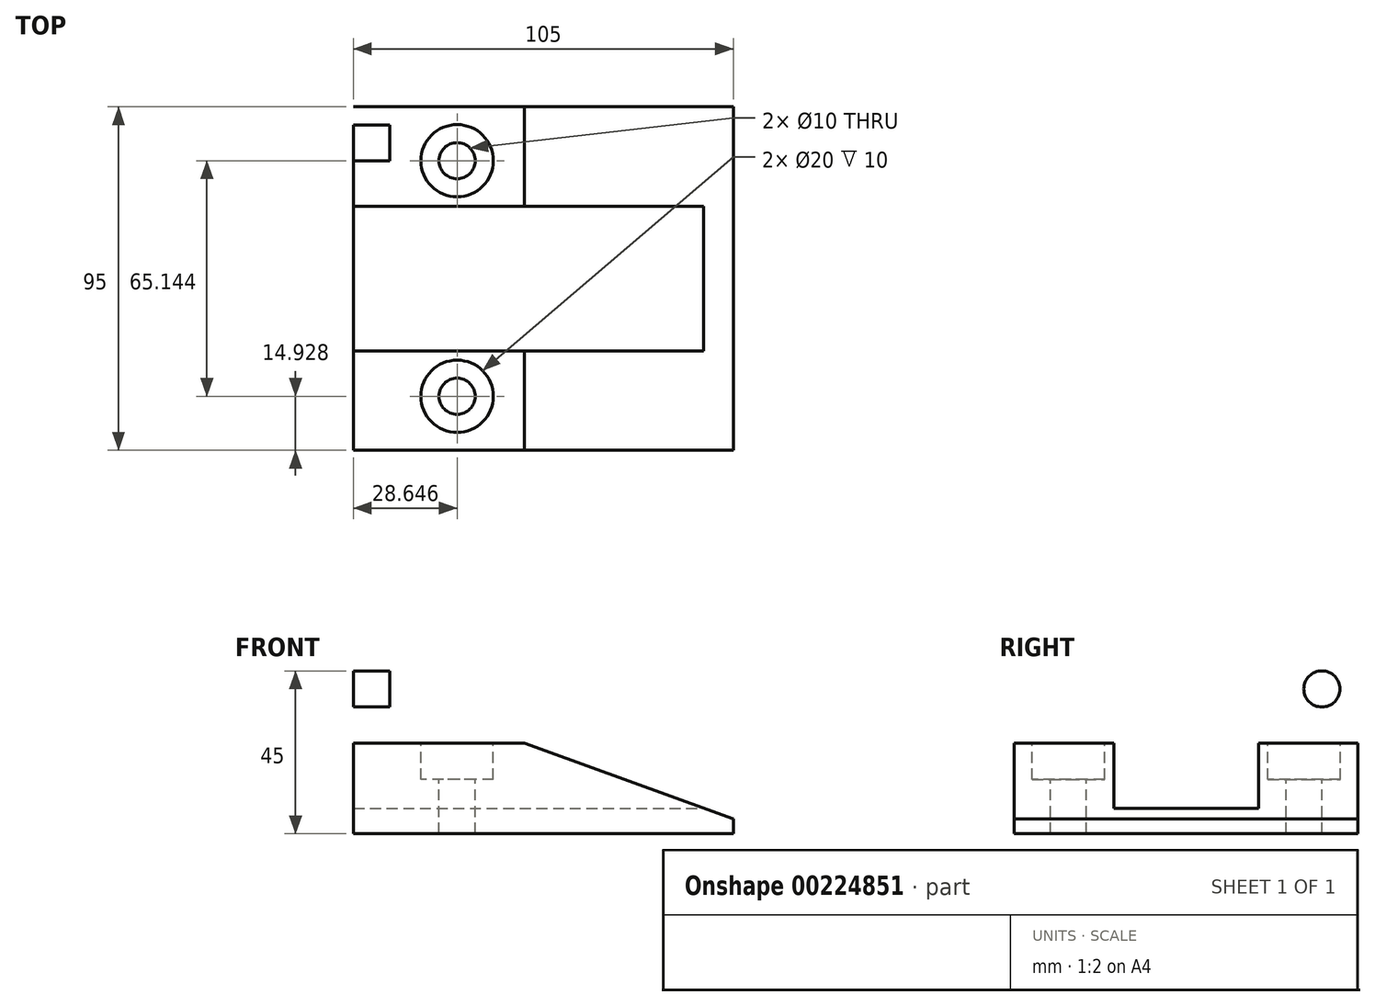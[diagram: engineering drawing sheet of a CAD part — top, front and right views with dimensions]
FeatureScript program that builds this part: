
annotation { "Feature Type Name" : "Feature", "Feature Type Description" : "" }
export const myFeature = defineFeature(function(context is Context, id is Id, definition is map)
    precondition{}
    {
        {
            var Q0;
            Q0=qCreatedBy(makeId("Top.planeOp"),FACE);
            var sketch = newSketch(context, id + "F0", { "sketchPlane" : qUnion([Q0])});
            skLineSegment(sketch, "E0.bottom", {"start": v(-10.05, 47.5) * mm, "end": v(-0.05, 47.5) * mm});
            skLineSegment(sketch, "E0.top", {"start": v(-10.05, -47.5) * mm, "end": v(-0.05, -47.5) * mm});
            skLineSegment(sketch, "E0.left", {"start": v(-10.05, 47.5) * mm, "end": v(-10.05, -47.5) * mm});
            skLineSegment(sketch, "E0.right", {"start": v(-0.05, 47.5) * mm, "end": v(-0.05, -47.5) * mm});
            skPoint(sketch, "E0.middle", {"position": v(-5.05, 0) * mm});
            skPoint(sketch, "E1.0", {"position": v(0, 0) * mm});
            skLineSegment(sketch, "E2", {"start": v(-3.1, 0) * mm, "end": v(-3.1, -20) * mm, "construction": true});
            skLineSegment(sketch, "E3.bottom", {"start": v(-0.05, -20) * mm, "end": v(37.25, -20) * mm});
            skLineSegment(sketch, "E3.top", {"start": v(-0.05, -47.5) * mm, "end": v(37.25, -47.5) * mm});
            skLineSegment(sketch, "E3.left", {"start": v(-0.05, -20) * mm, "end": v(-0.05, -47.5) * mm});
            skLineSegment(sketch, "E3.right", {"start": v(37.25, -20) * mm, "end": v(37.25, -47.5) * mm});
            skLineSegment(sketch, "E4", {"start": v(-3.1, 0) * mm, "end": v(63.94, 0) * mm, "construction": true});
            skLineSegment(sketch, "E5.MirrorCS", {"start": v(-0.05, 20) * mm, "end": v(37.25, 20) * mm});
            skLineSegment(sketch, "E6.MirrorCS", {"start": v(-0.05, 47.5) * mm, "end": v(37.25, 47.5) * mm});
            skLineSegment(sketch, "E7.MirrorCS", {"start": v(37.25, 20) * mm, "end": v(37.25, 47.5) * mm});
            skLineSegment(sketch, "E8", {"start": v(37.25, -47.5) * mm, "end": v(94.95, -47.5) * mm});
            skLineSegment(sketch, "E9.MirrorCS", {"start": v(37.25, 47.5) * mm, "end": v(94.95, 47.5) * mm});
            skLineSegment(sketch, "E10", {"start": v(94.95, 47.5) * mm, "end": v(94.95, -47.5) * mm});
            skLineSegment(sketch, "E11", {"start": v(-0.05, 32.57) * mm, "end": v(18.6, 32.57) * mm, "construction": true});
            skPoint(sketch, "E12", {"position": v(18.6, 32.57) * mm});
            skPoint(sketch, "E13.MirrorP", {"position": v(18.6, -32.57) * mm});
            skSolve(sketch);
        }
        {
            var Q0;
            {var subQ4=sQuery(id+"F0.wireOp",EDGE,"E0.bottom");Q0=makeQuery(id+"F0.imprint","IMPRINT",FACE,{"disambiguationData":[TD([[makeQuery(id+"F0.imprint","IMPRINT",EDGE,{"derivedFrom":subQ4}),-1.0]])]});}
            extrude(context, id + "F1", {"entities" : qUnion([Q0]), "depth" : 50 * mm});
        }
        {
            var Q0;
            {var subQ2=sQuery(id+"F0.wireOp",EDGE,"E3.bottom");Q0=makeQuery(id+"F0.imprint","IMPRINT",FACE,{"disambiguationData":[TD([[makeQuery(id+"F0.imprint","IMPRINT",EDGE,{"derivedFrom":subQ2}),-1.0]])]});}
            var Q1;
            {var subQ2=sQuery(id+"F0.wireOp",EDGE,"E5.MirrorCS");Q1=makeQuery(id+"F0.imprint","IMPRINT",FACE,{"disambiguationData":[TD([[makeQuery(id+"F0.imprint","IMPRINT",EDGE,{"derivedFrom":subQ2}),1.0]])]});}
            extrude(context, id + "F2", {"entities" : qUnion([Q0, Q1]), "operationType" : NewBodyOperationType.ADD, "depth" : 25 * mm});
        }
        {
            var Q0;
            {var subQ1=sQuery(id+"F0.wireOp",EDGE,"E3.bottom");Q0=makeQuery(id+"F0.imprint","IMPRINT",FACE,{"disambiguationData":[TD([[makeQuery(id+"F0.imprint","IMPRINT",EDGE,{"derivedFrom":subQ1}),1.0]])]});}
            extrude(context, id + "F3", {"entities" : qUnion([Q0]), "operationType" : NewBodyOperationType.ADD, "depth" : 4 * mm});
        }
        {
            var Q0;
            Q0=makeQuery(id+"F3.boolean.opBoolean","MERGE",FACE,{"derivedFrom":[makeQuery(id+"F2.boolean.opBoolean","MERGE",FACE,{"derivedFrom":[makeQuery(id+"F1.opExtrude","SWEPT_FACE",FACE,{"disambiguationData":[OSD([sQuery(id+"F0.wireOp",EDGE,"E0.top")])]}),makeQuery(id+"F2.opExtrude","SWEPT_FACE",FACE,{"disambiguationData":[OSD([sQuery(id+"F0.wireOp",EDGE,"E3.top")])]})]}),makeQuery(id+"F3.opExtrude","SWEPT_FACE",FACE,{"disambiguationData":[OSD([sQuery(id+"F0.wireOp",EDGE,"E8")])]})]});
            var sketch = newSketch(context, id + "F4", { "sketchPlane" : qUnion([Q0])});
            skLineSegment(sketch, "E14.0", {"start": v(-0.05, 25) * mm, "end": v(37.25, 25) * mm});
            skLineSegment(sketch, "E15.0", {"start": v(37.25, 4) * mm, "end": v(94.95, 4) * mm});
            skLineSegment(sketch, "E16", {"start": v(37.25, 25) * mm, "end": v(94.95, 4) * mm});
            skLineSegment(sketch, "E17", {"start": v(37.25, 25) * mm, "end": v(37.25, 4) * mm});
            skSolve(sketch);
        }
        {
            var Q0;
            Q0=makeQuery(id+"F4.imprint","IMPRINT",FACE,{"disambiguationData":[TD([[makeQuery(id+"F4.imprint","IMPRINT",EDGE,{"derivedFrom":sQuery(id+"F4.wireOp",EDGE,"E15.0")}),1.0]])]});
            extrude(context, id + "F5", {"entities" : qUnion([Q0]), "oppositeDirection" : true, "depth" : 27.5 * mm});
        }
        {
            var Q0;
            Q0=makeQuery(id+"F5.opExtrude","SWEPT_BODY",BODY,{"disambiguationData":[OSD([sQuery(id+"F4.wireOp",EDGE,"E15.0"),sQuery(id+"F4.wireOp",EDGE,"E16"),sQuery(id+"F4.wireOp",EDGE,"E17")])]});
            var Q1;
            Q1=qCreatedBy(makeId("Front.planeOp"),FACE);
            mirror(context, id + "F6", {"operationType" : NewBodyOperationType.ADD, "entities" : qUnion([Q0]), "mirrorPlane" : qUnion([Q1])});
        }
        {
            var Q0;
            Q0=makeQuery(id+"F1.opExtrude","CAP_EDGE",EDGE,{"disambiguationData":[OSD([sQuery(id+"F0.wireOp",EDGE,"E0.top")])],"isStart":false});
            var Q1;
            Q1=makeQuery(id+"F1.opExtrude","CAP_EDGE",EDGE,{"disambiguationData":[OSD([sQuery(id+"F0.wireOp",EDGE,"E0.bottom")])],"isStart":false});
            fillet(context, id + "F7", {"entities" : qUnion([Q0, Q1]), "radius" : 10 * mm, "tangentPropagation" : true, "allowEdgeOverflow" : false});
        }
        {
            var Q0;
            Q0=makeQuery(id+"F1.opExtrude","SWEPT_FACE",FACE,{"disambiguationData":[OSD([sQuery(id+"F0.wireOp",EDGE,"E0.right")])]});
            var sketch = newSketch(context, id + "F8", { "sketchPlane" : qUnion([Q0])});
            skLineSegment(sketch, "E18", {"start": v(0, 0) * mm, "end": v(0, 50) * mm, "construction": true});
            skArc(sketch, "E19.0", {"start": v(-37.5, 50) * mm, "mid": v(-44.57, 47.07) * mm, "end": v(-47.5, 40) * mm});
            skCircle(sketch, "E20", {"center": v(-37.5, 40) * mm, "radius": 5 * mm});
            skCircle(sketch, "E21.MirrorC", {"center": v(37.5, 40) * mm, "radius": 5 * mm});
            skSolve(sketch);
        }
        {
            var Q0;
            Q0=makeQuery(id+"F8.imprint","IMPRINT",FACE,{"disambiguationData":[TD([[makeQuery(id+"F8.imprint","IMPRINT",EDGE,{"derivedFrom":sQuery(id+"F8.wireOp",EDGE,"E20")}),1.0]])]});
            var Q1;
            Q1=makeQuery(id+"F8.imprint","IMPRINT",FACE,{"disambiguationData":[TD([[makeQuery(id+"F8.imprint","IMPRINT",EDGE,{"derivedFrom":sQuery(id+"F8.wireOp",EDGE,"E21.MirrorC")}),-1.0]])]});
            extrude(context, id + "F9", {"entities" : qUnion([Q0, Q1]), "operationType" : NewBodyOperationType.REMOVE, "oppositeDirection" : true, "depth" : 25 * mm});
        }
        {
            var Q0;
            Q0=makeQuery(id+"F3.opExtrude","CAP_FACE",FACE,{"disambiguationData":[OSD([sQuery(id+"F0.wireOp",EDGE,"E0.right"),sQuery(id+"F0.wireOp",EDGE,"E3.bottom"),sQuery(id+"F0.wireOp",EDGE,"E3.right"),sQuery(id+"F0.wireOp",EDGE,"E5.MirrorCS"),sQuery(id+"F0.wireOp",EDGE,"E7.MirrorCS"),sQuery(id+"F0.wireOp",EDGE,"E8"),sQuery(id+"F0.wireOp",EDGE,"E9.MirrorCS"),sQuery(id+"F0.wireOp",EDGE,"E10")])],"isStart":false});
            var sketch = newSketch(context, id + "F10", { "sketchPlane" : qUnion([Q0])});
            skLineSegment(sketch, "E22.0", {"start": v(-0.05, 20) * mm, "end": v(94.95, 20) * mm});
            skLineSegment(sketch, "E22.1", {"start": v(-0.05, -20) * mm, "end": v(94.95, -20) * mm});
            skLineSegment(sketch, "E23", {"start": v(86.7, 20) * mm, "end": v(86.7, -20) * mm});
            skSolve(sketch);
        }
        {
            var Q0;
            Q0=makeQuery(id+"F6.boolean.opBoolean","MERGE",FACE,{"derivedFrom":[makeQuery(id+"F2.opExtrude","SWEPT_FACE",FACE,{"disambiguationData":[OSD([sQuery(id+"F0.wireOp",EDGE,"E3.bottom")])]}),makeQuery(id+"F5.opExtrude","CAP_FACE",FACE,{"disambiguationData":[OSD([sQuery(id+"F4.wireOp",EDGE,"E15.0"),sQuery(id+"F4.wireOp",EDGE,"E16"),sQuery(id+"F4.wireOp",EDGE,"E17")])],"isStart":false})]});
            var sketch = newSketch(context, id + "F11", { "sketchPlane" : qUnion([Q0])});
            skPoint(sketch, "E24", {"position": v(-86.7, 4) * mm});
            skLineSegment(sketch, "E25", {"start": v(-86.7, 4) * mm, "end": v(-86.7, 7) * mm});
            skLineSegment(sketch, "E26.0", {"start": v(-37.25, 25) * mm, "end": v(-94.95, 4) * mm});
            skLineSegment(sketch, "E27.0", {"start": v(0.05, 4) * mm, "end": v(-94.95, 4) * mm});
            skSolve(sketch);
        }
        {
            var Q0;
            {var subQ0=sQuery(id+"F11.wireOp",EDGE,"E25");Q0=makeQuery(id+"F11.imprint","IMPRINT",FACE,{"disambiguationData":[TD([[makeQuery(id+"F11.imprint","IMPRINT",EDGE,{"derivedFrom":subQ0}),1.0]])]});}
            extrude(context, id + "F12", {"entities" : qUnion([Q0]), "operationType" : NewBodyOperationType.ADD, "depth" : 40 * mm});
        }
        {
            var Q0;
            {var subQ2=sQuery(id+"F10.wireOp",EDGE,"E23");Q0=makeQuery(id+"F10.imprint","IMPRINT",FACE,{"disambiguationData":[TD([[makeQuery(id+"F10.imprint","IMPRINT",EDGE,{"derivedFrom":subQ2}),-1.0]])]});}
            extrude(context, id + "F13", {"entities" : qUnion([Q0]), "operationType" : NewBodyOperationType.ADD, "depth" : 3 * mm});
        }
        {
            var Q0;
            Q0=makeQuery(id+"F2.opExtrude","CAP_FACE",FACE,{"disambiguationData":[OSD([sQuery(id+"F0.wireOp",EDGE,"E0.right"),sQuery(id+"F0.wireOp",EDGE,"E3.bottom"),sQuery(id+"F0.wireOp",EDGE,"E3.top"),sQuery(id+"F0.wireOp",EDGE,"E3.right")])],"isStart":false});
            var sketch = newSketch(context, id + "F14", { "sketchPlane" : qUnion([Q0])});
            skPoint(sketch, "E28", {"position": v(18.6, -32.57) * mm});
            skPoint(sketch, "E29", {"position": v(18.6, 32.57) * mm});
            skSolve(sketch);
        }
        {
            var Q0;
            Q0=sQuery(id+"F14.wireOp",VERTEX,"E28");
            var Q1;
            Q1=sQuery(id+"F14.wireOp",VERTEX,"E29");
            var Q2;
            Q2=makeQuery(id+"F1.opExtrude","SWEPT_BODY",BODY,{"disambiguationData":[OSD([sQuery(id+"F0.wireOp",EDGE,"E0.bottom"),sQuery(id+"F0.wireOp",EDGE,"E0.top"),sQuery(id+"F0.wireOp",EDGE,"E0.left"),sQuery(id+"F0.wireOp",EDGE,"E0.right")])]});
            hole(context, id + "F15", {"style" : HoleStyle.C_BORE, "endStyle" : HoleEndStyle.THROUGH, "holeDiameter" : 10 * mm, "cBoreDiameter" : 20 * mm, "cBoreDepth" : 10 * mm, "locations" : qUnion([Q0, Q1]), "scope" : qUnion([Q2]), "tappedDepth" : 12 * mm, "tapClearance" : 3});
        }
    });
